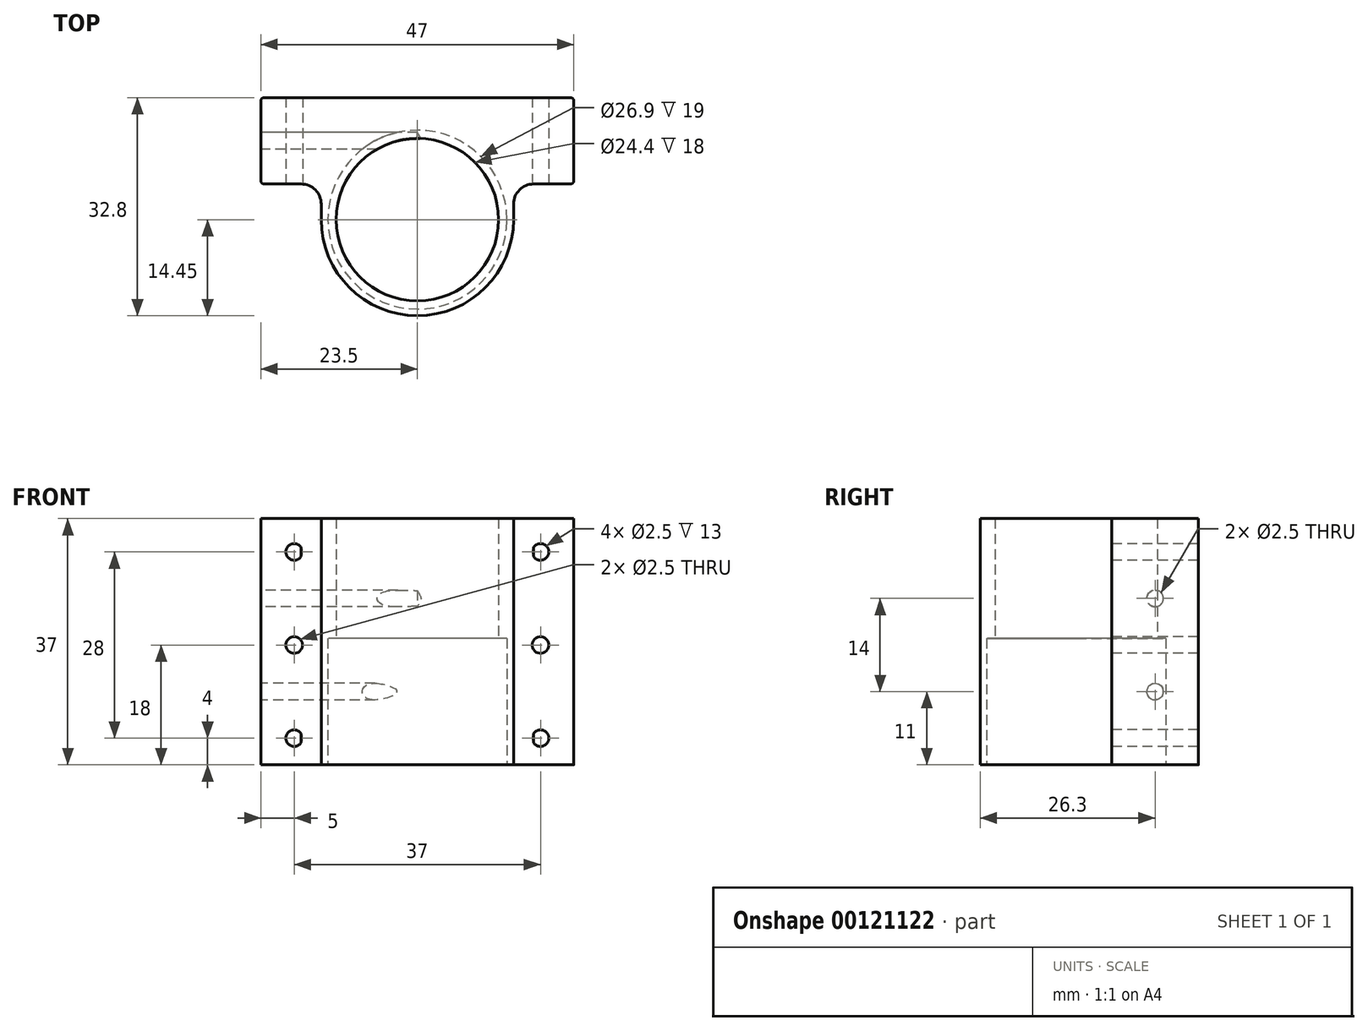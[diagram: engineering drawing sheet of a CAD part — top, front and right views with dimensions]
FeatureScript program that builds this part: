
annotation { "Feature Type Name" : "Feature", "Feature Type Description" : "" }
export const myFeature = defineFeature(function(context is Context, id is Id, definition is map)
    precondition{}
    {
        {
            var Q0;
            Q0=qCreatedBy(makeId("Top.planeOp"),FACE);
            var sketch = newSketch(context, id + "F0", { "sketchPlane" : qUnion([Q0])});
            skArc(sketch, "E0", {"start": v(-14.45, 0) * mm, "mid": v(0, -14.45) * mm, "end": v(14.45, 0) * mm});
            skCircle(sketch, "E1", {"center": v(0, 0) * mm, "radius": 13.45 * mm});
            skLineSegment(sketch, "E2", {"start": v(-23.5, 18.35) * mm, "end": v(0, 18.35) * mm});
            skLineSegment(sketch, "E3", {"start": v(-23.5, 18.35) * mm, "end": v(-23.5, 5.35) * mm});
            skLineSegment(sketch, "E4", {"start": v(-23.5, 5.35) * mm, "end": v(-14.45, 5.35) * mm});
            skLineSegment(sketch, "E5", {"start": v(-14.45, 0) * mm, "end": v(-14.45, 5.35) * mm});
            skPoint(sketch, "E6.start.orphan", {"position": v(-17.36, 0) * mm});
            skLineSegment(sketch, "E7.MirrorCS", {"start": v(14.45, 0) * mm, "end": v(14.45, 5.35) * mm});
            skLineSegment(sketch, "E8.MirrorCS", {"start": v(23.5, 5.35) * mm, "end": v(14.45, 5.35) * mm});
            skLineSegment(sketch, "E9.MirrorCS", {"start": v(23.5, 18.35) * mm, "end": v(0, 18.35) * mm});
            skLineSegment(sketch, "E10.MirrorCS", {"start": v(23.5, 18.35) * mm, "end": v(23.5, 5.35) * mm});
            skSolve(sketch);
        }
        {
            var Q0;
            Q0=makeQuery(id+"F0.imprint","IMPRINT",FACE,{"disambiguationData":[TD([[makeQuery(id+"F0.imprint","IMPRINT",EDGE,{"derivedFrom":sQuery(id+"F0.wireOp",EDGE,"E0")}),1.0]])]});
            extrude(context, id + "F1", {"entities" : qUnion([Q0]), "depth" : 19 * mm});
        }
        {
            var Q0;
            Q0=makeQuery(id+"F1.opExtrude","SWEPT_EDGE",EDGE,{"disambiguationData":[OSD([sQuery(id+"F0.wireOp",EDGE,"E3"),sQuery(id+"F0.wireOp",EDGE,"E4")])]});
            var Q1;
            Q1=makeQuery(id+"F1.opExtrude","SWEPT_EDGE",EDGE,{"disambiguationData":[OSD([sQuery(id+"F0.wireOp",EDGE,"E2"),sQuery(id+"F0.wireOp",EDGE,"E3")])]});
            var Q2;
            Q2=makeQuery(id+"F1.opExtrude","SWEPT_EDGE",EDGE,{"disambiguationData":[OSD([sQuery(id+"F0.wireOp",EDGE,"E8.MirrorCS"),sQuery(id+"F0.wireOp",EDGE,"E10.MirrorCS")])]});
            var Q3;
            Q3=makeQuery(id+"F1.opExtrude","SWEPT_EDGE",EDGE,{"disambiguationData":[OSD([sQuery(id+"F0.wireOp",EDGE,"E9.MirrorCS"),sQuery(id+"F0.wireOp",EDGE,"E10.MirrorCS")])]});
            fillet(context, id + "F2", {"entities" : qUnion([Q0, Q1, Q2, Q3]), "radius" : 0.5 * mm, "tangentPropagation" : true, "allowEdgeOverflow" : false});
        }
        {
            var Q0;
            Q0=makeQuery(id+"F1.opExtrude","SWEPT_EDGE",EDGE,{"disambiguationData":[OSD([sQuery(id+"F0.wireOp",EDGE,"E7.MirrorCS"),sQuery(id+"F0.wireOp",EDGE,"E8.MirrorCS")])]});
            var Q1;
            Q1=makeQuery(id+"F1.opExtrude","SWEPT_EDGE",EDGE,{"disambiguationData":[OSD([sQuery(id+"F0.wireOp",EDGE,"E4"),sQuery(id+"F0.wireOp",EDGE,"E5")])]});
            fillet(context, id + "F3", {"entities" : qUnion([Q0, Q1]), "radius" : 3 * mm, "tangentPropagation" : true, "allowEdgeOverflow" : false});
        }
        {
            var Q0;
            {var subQ0=sQuery(id+"F0.wireOp",EDGE,"E3");var subQ1=sQuery(id+"F0.wireOp",EDGE,"E9.MirrorCS");var subQ2=sQuery(id+"F0.wireOp",EDGE,"E2");var subQ3=sQuery(id+"F0.wireOp",EDGE,"E1");var subQ4=sQuery(id+"F0.wireOp",EDGE,"E0");var subQ5=sQuery(id+"F0.wireOp",EDGE,"E4");var subQ6=sQuery(id+"F0.wireOp",EDGE,"E5");var subQ7=sQuery(id+"F0.wireOp",EDGE,"E7.MirrorCS");var subQ8=sQuery(id+"F0.wireOp",EDGE,"E8.MirrorCS");Q0=makeQuery(id+"FAADP7nb1SWJzTk_1.hole-4.boolean.opBoolean","SPLIT",FACE,{"disambiguationData":[TD([makeQuery(id+"F1.opExtrude","SWEPT_FACE",FACE,{"disambiguationData":[OSD([subQ4])]})])],"derivedFrom":makeQuery(id+"F1.opExtrude","CAP_FACE",FACE,{"disambiguationData":[OSD([subQ4,subQ3,subQ2,subQ0,subQ5,subQ6,subQ7,subQ8,subQ1,sQuery(id+"F0.wireOp",EDGE,"E10.MirrorCS")])],"isStart":false})});}
            var sketch = newSketch(context, id + "F4", { "sketchPlane" : qUnion([Q0])});
            skLineSegment(sketch, "E11", {"start": v(-23, 18.35) * mm, "end": v(0, 18.35) * mm});
            skLineSegment(sketch, "E12", {"start": v(-23.5, 17.85) * mm, "end": v(-23.5, 5.85) * mm});
            skLineSegment(sketch, "E13", {"start": v(-23, 5.35) * mm, "end": v(-17.45, 5.35) * mm});
            skArc(sketch, "E14", {"start": v(-23.5, 17.85) * mm, "mid": v(-23.35, 18.2) * mm, "end": v(-23, 18.35) * mm});
            skArc(sketch, "E15", {"start": v(-23.5, 5.85) * mm, "mid": v(-23.35, 5.5) * mm, "end": v(-23, 5.35) * mm});
            skArc(sketch, "E16", {"start": v(-17.45, 5.35) * mm, "mid": v(-15.33, 4.47) * mm, "end": v(-14.45, 2.35) * mm});
            skLineSegment(sketch, "E17", {"start": v(-14.45, 2.35) * mm, "end": v(-14.45, 0) * mm});
            skArc(sketch, "E18", {"start": v(-14.45, 0) * mm, "mid": v(-10.22, -10.22) * mm, "end": v(0, -14.45) * mm});
            skArc(sketch, "E19.MirrorCS", {"start": v(14.45, 0) * mm, "mid": v(10.22, -10.22) * mm, "end": v(0, -14.45) * mm});
            skLineSegment(sketch, "E20.MirrorCS", {"start": v(14.45, 2.35) * mm, "end": v(14.45, 0) * mm});
            skArc(sketch, "E21.MirrorCS", {"start": v(17.45, 5.35) * mm, "mid": v(15.33, 4.47) * mm, "end": v(14.45, 2.35) * mm});
            skLineSegment(sketch, "E22.MirrorCS", {"start": v(23, 5.35) * mm, "end": v(17.45, 5.35) * mm});
            skArc(sketch, "E23.MirrorCS", {"start": v(23.5, 5.85) * mm, "mid": v(23.35, 5.5) * mm, "end": v(23, 5.35) * mm});
            skLineSegment(sketch, "E24.MirrorCS", {"start": v(23, 18.35) * mm, "end": v(0, 18.35) * mm});
            skLineSegment(sketch, "E25.MirrorCS", {"start": v(23.5, 17.85) * mm, "end": v(23.5, 5.85) * mm});
            skArc(sketch, "E26.MirrorCS", {"start": v(23.5, 17.85) * mm, "mid": v(23.35, 18.2) * mm, "end": v(23, 18.35) * mm});
            skCircle(sketch, "E27", {"center": v(0, 0) * mm, "radius": 12.2 * mm});
            skSolve(sketch);
        }
        {
            var Q0;
            Q0 = qSketchRegion(id + "F4", true);
            extrude(context, id + "F5", {"entities" : qUnion([Q0]), "operationType" : NewBodyOperationType.ADD, "depth" : 18 * mm});
        }
        {
            var Q0;
            Q0=makeQuery(id+"F5.boolean.opBoolean","MERGE",FACE,{"derivedFrom":[makeQuery(id+"F1.opExtrude","SWEPT_FACE",FACE,{"disambiguationData":[OSD([sQuery(id+"F0.wireOp",EDGE,"E4")])]}),makeQuery(id+"F5.opExtrude","SWEPT_FACE",FACE,{"disambiguationData":[OSD([sQuery(id+"F4.wireOp",EDGE,"E13")])]})]});
            var sketch = newSketch(context, id + "F6", { "sketchPlane" : qUnion([Q0])});
            skPoint(sketch, "E28", {"position": v(-18.5, 32) * mm});
            skPoint(sketch, "E29", {"position": v(-18.5, 18) * mm});
            skPoint(sketch, "E30", {"position": v(-18.5, 4) * mm});
            skPoint(sketch, "E31", {"position": v(18.5, 32) * mm});
            skPoint(sketch, "E32", {"position": v(18.5, 18) * mm});
            skPoint(sketch, "E33", {"position": v(18.5, 4) * mm});
            skSolve(sketch);
        }
        {
            var Q0;
            Q0=sQuery(id+"F6.wireOp",VERTEX,"E28");
            var Q1;
            Q1=sQuery(id+"F6.wireOp",VERTEX,"E29");
            var Q2;
            Q2=sQuery(id+"F6.wireOp",VERTEX,"E30");
            var Q3;
            Q3=sQuery(id+"F6.wireOp",VERTEX,"E33");
            var Q4;
            Q4=sQuery(id+"F6.wireOp",VERTEX,"E32");
            var Q5;
            Q5=sQuery(id+"F6.wireOp",VERTEX,"E31");
            var Q6;
            Q6=makeQuery(id+"F1.opExtrude","SWEPT_BODY",BODY,{"disambiguationData":[OSD([sQuery(id+"F0.wireOp",EDGE,"E0"),sQuery(id+"F0.wireOp",EDGE,"E1"),sQuery(id+"F0.wireOp",EDGE,"E2"),sQuery(id+"F0.wireOp",EDGE,"E3"),sQuery(id+"F0.wireOp",EDGE,"E4"),sQuery(id+"F0.wireOp",EDGE,"E5"),sQuery(id+"F0.wireOp",EDGE,"E7.MirrorCS"),sQuery(id+"F0.wireOp",EDGE,"E8.MirrorCS"),sQuery(id+"F0.wireOp",EDGE,"E9.MirrorCS"),sQuery(id+"F0.wireOp",EDGE,"E10.MirrorCS")])]});
            hole(context, id + "F7", {"style" : HoleStyle.SIMPLE, "endStyle" : HoleEndStyle.BLIND, "holeDiameter" : 2.5 * mm, "holeDepth" : 50 * mm, "locations" : qUnion([Q0, Q1, Q2, Q3, Q4, Q5]), "scope" : qUnion([Q6])});
        }
        {
            var Q0;
            Q0=makeQuery(id+"F5.boolean.opBoolean","MERGE",FACE,{"derivedFrom":[makeQuery(id+"F1.opExtrude","SWEPT_FACE",FACE,{"disambiguationData":[OSD([sQuery(id+"F0.wireOp",EDGE,"E3")])]}),makeQuery(id+"F5.opExtrude","SWEPT_FACE",FACE,{"disambiguationData":[OSD([sQuery(id+"F4.wireOp",EDGE,"E12")])]})]});
            var sketch = newSketch(context, id + "F8", { "sketchPlane" : qUnion([Q0])});
            skPoint(sketch, "E34", {"position": v(-11.85, 25) * mm});
            skPoint(sketch, "E35", {"position": v(-11.85, 11) * mm});
            skSolve(sketch);
        }
        {
            var Q0;
            Q0=sQuery(id+"F8.wireOp",VERTEX,"E34");
            var Q1;
            Q1=sQuery(id+"F8.wireOp",VERTEX,"E35");
            var Q2;
            Q2=makeQuery(id+"F1.opExtrude","SWEPT_BODY",BODY,{"disambiguationData":[OSD([sQuery(id+"F0.wireOp",EDGE,"E0"),sQuery(id+"F0.wireOp",EDGE,"E1"),sQuery(id+"F0.wireOp",EDGE,"E2"),sQuery(id+"F0.wireOp",EDGE,"E3"),sQuery(id+"F0.wireOp",EDGE,"E4"),sQuery(id+"F0.wireOp",EDGE,"E5"),sQuery(id+"F0.wireOp",EDGE,"E7.MirrorCS"),sQuery(id+"F0.wireOp",EDGE,"E8.MirrorCS"),sQuery(id+"F0.wireOp",EDGE,"E9.MirrorCS"),sQuery(id+"F0.wireOp",EDGE,"E10.MirrorCS")])]});
            hole(context, id + "F9", {"style" : HoleStyle.SIMPLE, "endStyle" : HoleEndStyle.BLIND, "holeDiameter" : 2.5 * mm, "holeDepth" : 23.5 * mm, "locations" : qUnion([Q0, Q1]), "scope" : qUnion([Q2])});
        }
    });
